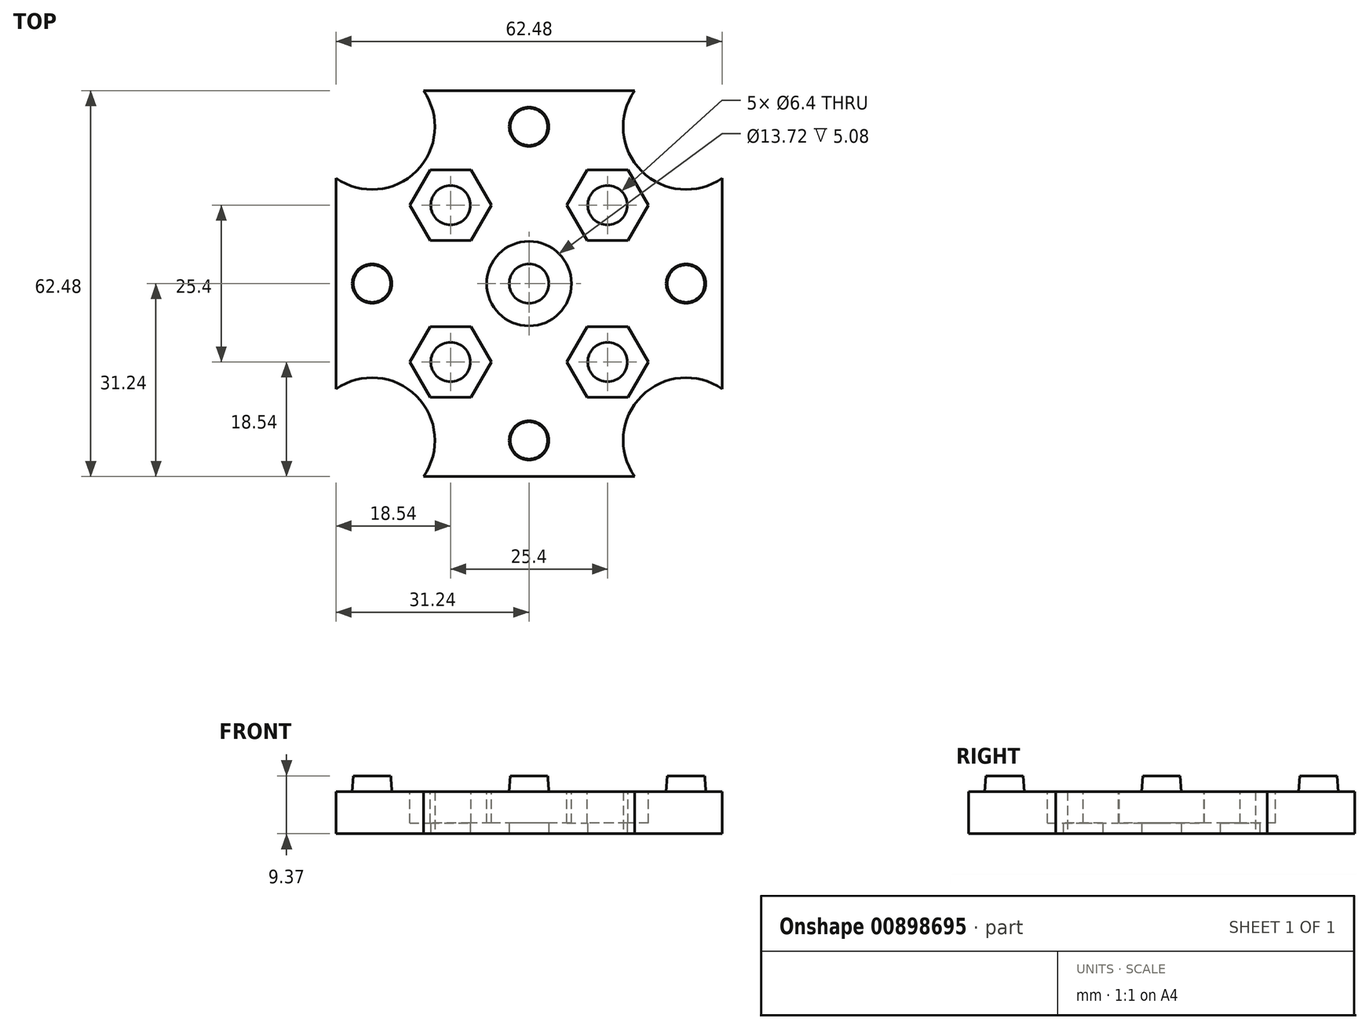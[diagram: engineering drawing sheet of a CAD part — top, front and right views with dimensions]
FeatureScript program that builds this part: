
annotation { "Feature Type Name" : "Feature", "Feature Type Description" : "" }
export const myFeature = defineFeature(function(context is Context, id is Id, definition is map)
    precondition{}
    {
        {
            var Q0;
            Q0=qCreatedBy(makeId("Top.planeOp"),FACE);
            var sketch = newSketch(context, id + "F0", { "sketchPlane" : qUnion([Q0])});
            skLineSegment(sketch, "E0.bottom", {"start": v(-25.4, 25.4) * mm, "end": v(25.4, 25.4) * mm, "construction": true});
            skLineSegment(sketch, "E0.top", {"start": v(-25.4, -25.4) * mm, "end": v(25.4, -25.4) * mm, "construction": true});
            skLineSegment(sketch, "E0.left", {"start": v(-25.4, 25.4) * mm, "end": v(-25.4, -25.4) * mm, "construction": true});
            skLineSegment(sketch, "E0.right", {"start": v(25.4, 25.4) * mm, "end": v(25.4, -25.4) * mm, "construction": true});
            skLineSegment(sketch, "E1", {"start": v(0, 25.4) * mm, "end": v(0, -25.4) * mm, "construction": true});
            skLineSegment(sketch, "E2", {"start": v(-25.4, 0) * mm, "end": v(25.4, 0) * mm, "construction": true});
            skCircle(sketch, "E3", {"center": v(-25.4, -25.4) * mm, "radius": 10.16 * mm});
            skArc(sketch, "E4", {"start": v(-31.24, 17.09) * mm, "mid": v(-18.22, 18.22) * mm, "end": v(-17.09, 31.24) * mm});
            skCircle(sketch, "E5", {"center": v(25.4, -25.4) * mm, "radius": 10.16 * mm});
            skCircle(sketch, "E6", {"center": v(25.4, 25.4) * mm, "radius": 10.16 * mm});
            skCircle(sketch, "E7", {"center": v(0, 0) * mm, "radius": 3.2 * mm});
            skCircle(sketch, "E8", {"center": v(-12.7, -12.7) * mm, "radius": 3.2 * mm});
            skCircle(sketch, "E9.0.1.0", {"center": v(-12.7, 12.7) * mm, "radius": 3.2 * mm});
            skCircle(sketch, "E9.1.0.0", {"center": v(12.7, -12.7) * mm, "radius": 3.2 * mm});
            skCircle(sketch, "E9.1.1.0", {"center": v(12.7, 12.7) * mm, "radius": 3.2 * mm});
            skLineSegment(sketch, "E9.direction1", {"start": v(-12.7, -12.7) * mm, "end": v(12.7, -12.7) * mm, "construction": true});
            skLineSegment(sketch, "E9.direction2", {"start": v(-12.7, -12.7) * mm, "end": v(-12.7, 12.7) * mm, "construction": true});
            skCircle(sketch, "E10", {"center": v(0, 0) * mm, "radius": 6.86 * mm});
            skCircle(sketch, "E11", {"center": v(-25.4, 0) * mm, "radius": 3.2 * mm});
            skCircle(sketch, "E12", {"center": v(0, 25.4) * mm, "radius": 3.2 * mm});
            skCircle(sketch, "E13", {"center": v(25.4, 0) * mm, "radius": 3.2 * mm});
            skCircle(sketch, "E14", {"center": v(0, -25.4) * mm, "radius": 3.2 * mm});
            skLineSegment(sketch, "E15.bottom", {"start": v(-31.24, 31.24) * mm, "end": v(31.24, 31.24) * mm});
            skLineSegment(sketch, "E15.top", {"start": v(-31.24, -31.24) * mm, "end": v(31.24, -31.24) * mm});
            skLineSegment(sketch, "E15.left", {"start": v(-31.24, 31.24) * mm, "end": v(-31.24, -31.24) * mm});
            skLineSegment(sketch, "E15.right", {"start": v(31.24, 31.24) * mm, "end": v(31.24, -31.24) * mm});
            skLineSegment(sketch, "E16", {"start": v(0, 25.4) * mm, "end": v(0, 31.24) * mm, "construction": true});
            skLineSegment(sketch, "E17", {"start": v(25.4, 0) * mm, "end": v(31.24, 0) * mm, "construction": true});
            skSolve(sketch);
        }
        {
            var Q0;
            {var subQ5=sQuery(id+"F0.wireOp",EDGE,"E4");Q0=makeQuery(id+"F0.imprint","IMPRINT",FACE,{"disambiguationData":[TD([[makeQuery(id+"F0.imprint","IMPRINT",EDGE,{"derivedFrom":subQ5}),-1.0]])]});}
            var Q1;
            Q1=makeQuery(id+"F0.imprint","IMPRINT",FACE,{"disambiguationData":[TD([[makeQuery(id+"F0.imprint","IMPRINT",EDGE,{"derivedFrom":sQuery(id+"F0.wireOp",EDGE,"E7")}),-1.0]])]});
            extrude(context, id + "F1", {"entities" : qUnion([Q0, Q1]), "depth" : 6.83 * mm, "offsetDistance" : 25.4 * mm});
        }
        {
            var Q0;
            Q0=makeQuery(id+"F0.imprint","IMPRINT",FACE,{"disambiguationData":[TD([[makeQuery(id+"F0.imprint","IMPRINT",EDGE,{"derivedFrom":sQuery(id+"F0.wireOp",EDGE,"E11")}),1.0]])]});
            var Q1;
            Q1=makeQuery(id+"F0.imprint","IMPRINT",FACE,{"disambiguationData":[TD([[makeQuery(id+"F0.imprint","IMPRINT",EDGE,{"derivedFrom":sQuery(id+"F0.wireOp",EDGE,"E14")}),1.0]])]});
            var Q2;
            Q2=makeQuery(id+"F0.imprint","IMPRINT",FACE,{"disambiguationData":[TD([[makeQuery(id+"F0.imprint","IMPRINT",EDGE,{"derivedFrom":sQuery(id+"F0.wireOp",EDGE,"E13")}),1.0]])]});
            var Q3;
            Q3=makeQuery(id+"F0.imprint","IMPRINT",FACE,{"disambiguationData":[TD([[makeQuery(id+"F0.imprint","IMPRINT",EDGE,{"derivedFrom":sQuery(id+"F0.wireOp",EDGE,"E12")}),1.0]])]});
            extrude(context, id + "F2", {"entities" : qUnion([Q0, Q1, Q2, Q3]), "operationType" : NewBodyOperationType.ADD, "depth" : 9.37 * mm, "offsetDistance" : 25.4 * mm});
        }
        {
            var Q0;
            Q0=makeQuery(id+"F1.opExtrude","CAP_FACE",FACE,{"disambiguationData":[OSD([sQuery(id+"F0.wireOp",EDGE,"E3"),sQuery(id+"F0.wireOp",EDGE,"E4"),sQuery(id+"F0.wireOp",EDGE,"E5"),sQuery(id+"F0.wireOp",EDGE,"E6"),sQuery(id+"F0.wireOp",EDGE,"E7"),sQuery(id+"F0.wireOp",EDGE,"E8"),sQuery(id+"F0.wireOp",EDGE,"E9.0.1.0"),sQuery(id+"F0.wireOp",EDGE,"E9.1.0.0"),sQuery(id+"F0.wireOp",EDGE,"E9.1.1.0"),sQuery(id+"F0.wireOp",EDGE,"E11"),sQuery(id+"F0.wireOp",EDGE,"E12"),sQuery(id+"F0.wireOp",EDGE,"E13"),sQuery(id+"F0.wireOp",EDGE,"E14"),sQuery(id+"F0.wireOp",EDGE,"E15.bottom"),sQuery(id+"F0.wireOp",EDGE,"E15.top"),sQuery(id+"F0.wireOp",EDGE,"E15.left"),sQuery(id+"F0.wireOp",EDGE,"E15.right")])],"isStart":false});
            var sketch = newSketch(context, id + "F3", { "sketchPlane" : qUnion([Q0])});
            skCircle(sketch, "E18.0", {"center": v(0, 0) * mm, "radius": 6.86 * mm});
            skCircle(sketch, "E19.0", {"center": v(12.7, 12.7) * mm, "radius": 3.2 * mm, "construction": true});
            skCircle(sketch, "E20.0", {"center": v(-12.7, 12.7) * mm, "radius": 3.2 * mm, "construction": true});
            skCircle(sketch, "E21.0", {"center": v(-12.7, -12.7) * mm, "radius": 3.2 * mm, "construction": true});
            skCircle(sketch, "E22.0", {"center": v(12.7, -12.7) * mm, "radius": 3.2 * mm, "construction": true});
            skCircle(sketch, "E23.cCircle", {"center": v(-12.7, 12.7) * mm, "radius": 6.6 * mm, "construction": true});
            skLineSegment(sketch, "E23.0", {"start": v(-6.1, 12.7) * mm, "end": v(-9.4, 6.98) * mm});
            skLineSegment(sketch, "E23.1", {"start": v(-9.4, 6.98) * mm, "end": v(-16, 6.98) * mm});
            skLineSegment(sketch, "E23.2", {"start": v(-16, 6.98) * mm, "end": v(-19.3, 12.7) * mm});
            skLineSegment(sketch, "E23.3", {"start": v(-19.3, 12.7) * mm, "end": v(-16, 18.42) * mm});
            skLineSegment(sketch, "E23.4", {"start": v(-16, 18.42) * mm, "end": v(-9.4, 18.42) * mm});
            skLineSegment(sketch, "E23.5", {"start": v(-9.4, 18.42) * mm, "end": v(-6.1, 12.7) * mm});
            skCircle(sketch, "E24.cCircle", {"center": v(12.7, 12.7) * mm, "radius": 6.6 * mm, "construction": true});
            skLineSegment(sketch, "E24.0", {"start": v(6.1, 12.7) * mm, "end": v(9.4, 18.42) * mm});
            skLineSegment(sketch, "E24.1", {"start": v(9.4, 18.42) * mm, "end": v(16, 18.42) * mm});
            skLineSegment(sketch, "E24.2", {"start": v(16, 18.42) * mm, "end": v(19.3, 12.7) * mm});
            skLineSegment(sketch, "E24.3", {"start": v(19.3, 12.7) * mm, "end": v(16, 6.98) * mm});
            skLineSegment(sketch, "E24.4", {"start": v(16, 6.98) * mm, "end": v(9.4, 6.98) * mm});
            skLineSegment(sketch, "E24.5", {"start": v(9.4, 6.98) * mm, "end": v(6.1, 12.7) * mm});
            skCircle(sketch, "E25.cCircle", {"center": v(-12.7, -12.7) * mm, "radius": 6.6 * mm, "construction": true});
            skLineSegment(sketch, "E25.0", {"start": v(-6.1, -12.7) * mm, "end": v(-9.4, -18.42) * mm});
            skLineSegment(sketch, "E25.1", {"start": v(-9.4, -18.42) * mm, "end": v(-16, -18.42) * mm});
            skLineSegment(sketch, "E25.2", {"start": v(-16, -18.42) * mm, "end": v(-19.3, -12.7) * mm});
            skLineSegment(sketch, "E25.3", {"start": v(-19.3, -12.7) * mm, "end": v(-16, -6.98) * mm});
            skLineSegment(sketch, "E25.4", {"start": v(-16, -6.98) * mm, "end": v(-9.4, -6.98) * mm});
            skLineSegment(sketch, "E25.5", {"start": v(-9.4, -6.98) * mm, "end": v(-6.1, -12.7) * mm});
            skCircle(sketch, "E26.cCircle", {"center": v(12.7, -12.7) * mm, "radius": 6.6 * mm, "construction": true});
            skLineSegment(sketch, "E26.0", {"start": v(6.1, -12.7) * mm, "end": v(9.4, -6.98) * mm});
            skLineSegment(sketch, "E26.1", {"start": v(9.4, -6.98) * mm, "end": v(16, -6.98) * mm});
            skLineSegment(sketch, "E26.2", {"start": v(16, -6.98) * mm, "end": v(19.3, -12.7) * mm});
            skLineSegment(sketch, "E26.3", {"start": v(19.3, -12.7) * mm, "end": v(16, -18.42) * mm});
            skLineSegment(sketch, "E26.4", {"start": v(16, -18.42) * mm, "end": v(9.4, -18.42) * mm});
            skLineSegment(sketch, "E26.5", {"start": v(9.4, -18.42) * mm, "end": v(6.1, -12.7) * mm});
            skSolve(sketch);
        }
        {
            var Q0;
            Q0=makeQuery(id+"F3.imprint","IMPRINT",FACE,{"disambiguationData":[TD([[makeQuery(id+"F3.imprint","IMPRINT",EDGE,{"derivedFrom":sQuery(id+"F3.wireOp",EDGE,"E23.0")}),-1.0]])]});
            var Q1;
            Q1=makeQuery(id+"F3.imprint","IMPRINT",FACE,{"disambiguationData":[TD([[makeQuery(id+"F3.imprint","IMPRINT",EDGE,{"derivedFrom":sQuery(id+"F3.wireOp",EDGE,"E24.0")}),-1.0]])]});
            var Q2;
            Q2=makeQuery(id+"F3.imprint","IMPRINT",FACE,{"disambiguationData":[TD([[makeQuery(id+"F3.imprint","IMPRINT",EDGE,{"derivedFrom":sQuery(id+"F3.wireOp",EDGE,"E25.0")}),-1.0]])]});
            var Q3;
            Q3=makeQuery(id+"F3.imprint","IMPRINT",FACE,{"disambiguationData":[TD([[makeQuery(id+"F3.imprint","IMPRINT",EDGE,{"derivedFrom":sQuery(id+"F3.wireOp",EDGE,"E26.0")}),-1.0]])]});
            var Q4;
            Q4=makeQuery(id+"F3.imprint","IMPRINT",FACE,{"disambiguationData":[TD([[makeQuery(id+"F3.imprint","IMPRINT",EDGE,{"derivedFrom":sQuery(id+"F3.wireOp",EDGE,"E18.0")}),1.0]])]});
            extrude(context, id + "F4", {"entities" : qUnion([Q0, Q1, Q2, Q3, Q4]), "operationType" : NewBodyOperationType.REMOVE, "oppositeDirection" : true, "depth" : 5.08 * mm, "offsetDistance" : 25.4 * mm});
        }
        {
            var Q0;
            Q0=makeQuery(id+"F2.opExtrude","CAP_EDGE",EDGE,{"disambiguationData":[OSD([sQuery(id+"F0.wireOp",EDGE,"E11")])],"isStart":false});
            var Q1;
            Q1=makeQuery(id+"F2.opExtrude","CAP_EDGE",EDGE,{"disambiguationData":[OSD([sQuery(id+"F0.wireOp",EDGE,"E12")])],"isStart":false});
            var Q2;
            Q2=makeQuery(id+"F2.opExtrude","CAP_EDGE",EDGE,{"disambiguationData":[OSD([sQuery(id+"F0.wireOp",EDGE,"E13")])],"isStart":false});
            var Q3;
            Q3=makeQuery(id+"F2.opExtrude","CAP_EDGE",EDGE,{"disambiguationData":[OSD([sQuery(id+"F0.wireOp",EDGE,"E14")])],"isStart":false});
            chamfer(context, id + "F5", {"entities" : qUnion([Q0, Q1, Q2, Q3]), "chamferType" : ChamferType.TWO_OFFSETS, "width1" : 0.18 * mm, "oppositeDirection" : false, "width2" : 2.54 * mm, "tangentPropagation" : true});
        }
    });
